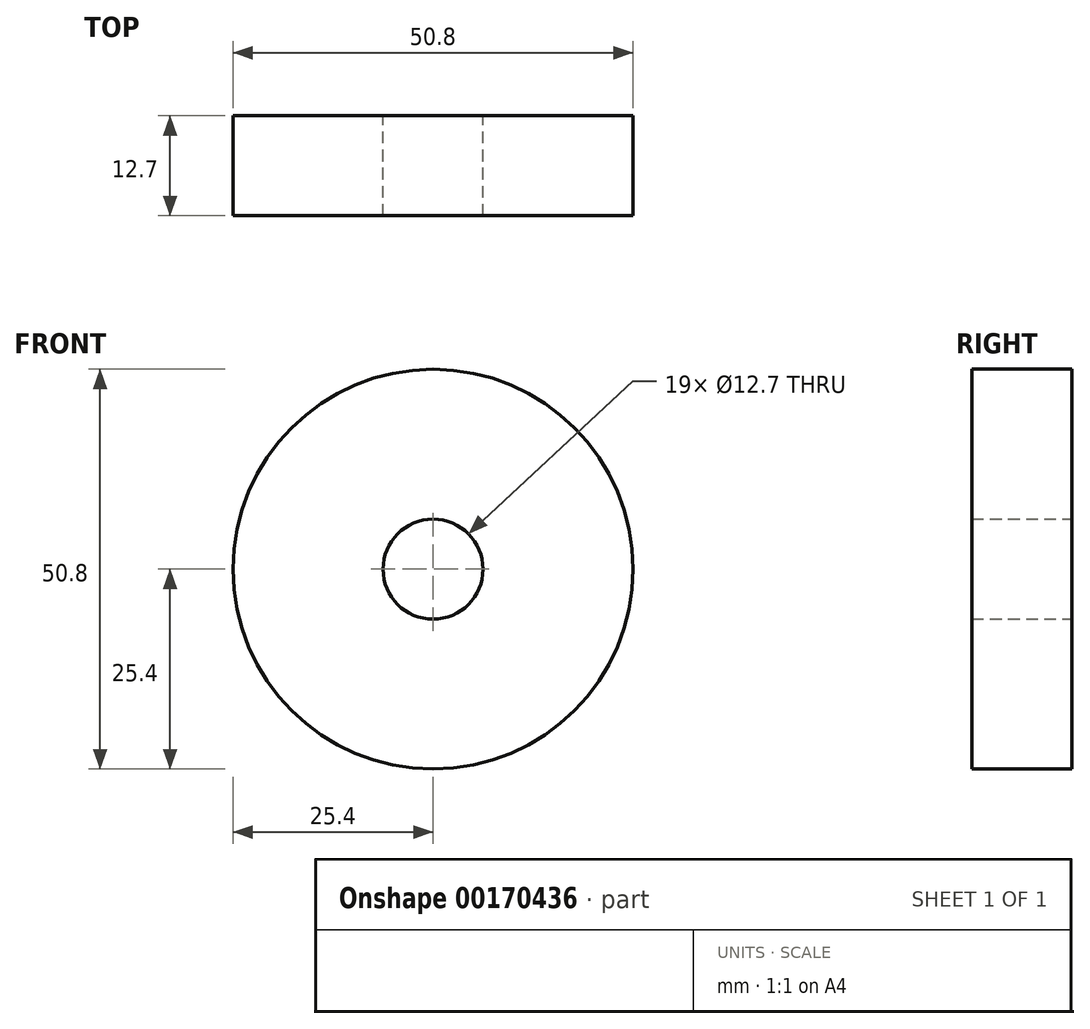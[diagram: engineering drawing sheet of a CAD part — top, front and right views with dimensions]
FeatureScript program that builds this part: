
annotation { "Feature Type Name" : "Feature", "Feature Type Description" : "" }
export const myFeature = defineFeature(function(context is Context, id is Id, definition is map)
    precondition{}
    {
        {
            var Q0;
            Q0=qCreatedBy(makeId("Front.planeOp"),FACE);
            var sketch = newSketch(context, id + "F0", { "sketchPlane" : qUnion([Q0])});
            skCircle(sketch, "E0", {"center": v(0, 0) * mm, "radius": 25.4 * mm});
            skCircle(sketch, "E1", {"center": v(0, 0) * mm, "radius": 6.35 * mm});
            skSolve(sketch);
        }
        {
            var Q0;
            Q0 = qSketchRegion(id + "F0", true);
            extrude(context, id + "F1", {"entities" : qUnion([Q0]), "depth" : 12.7 * mm});
        }
    });
